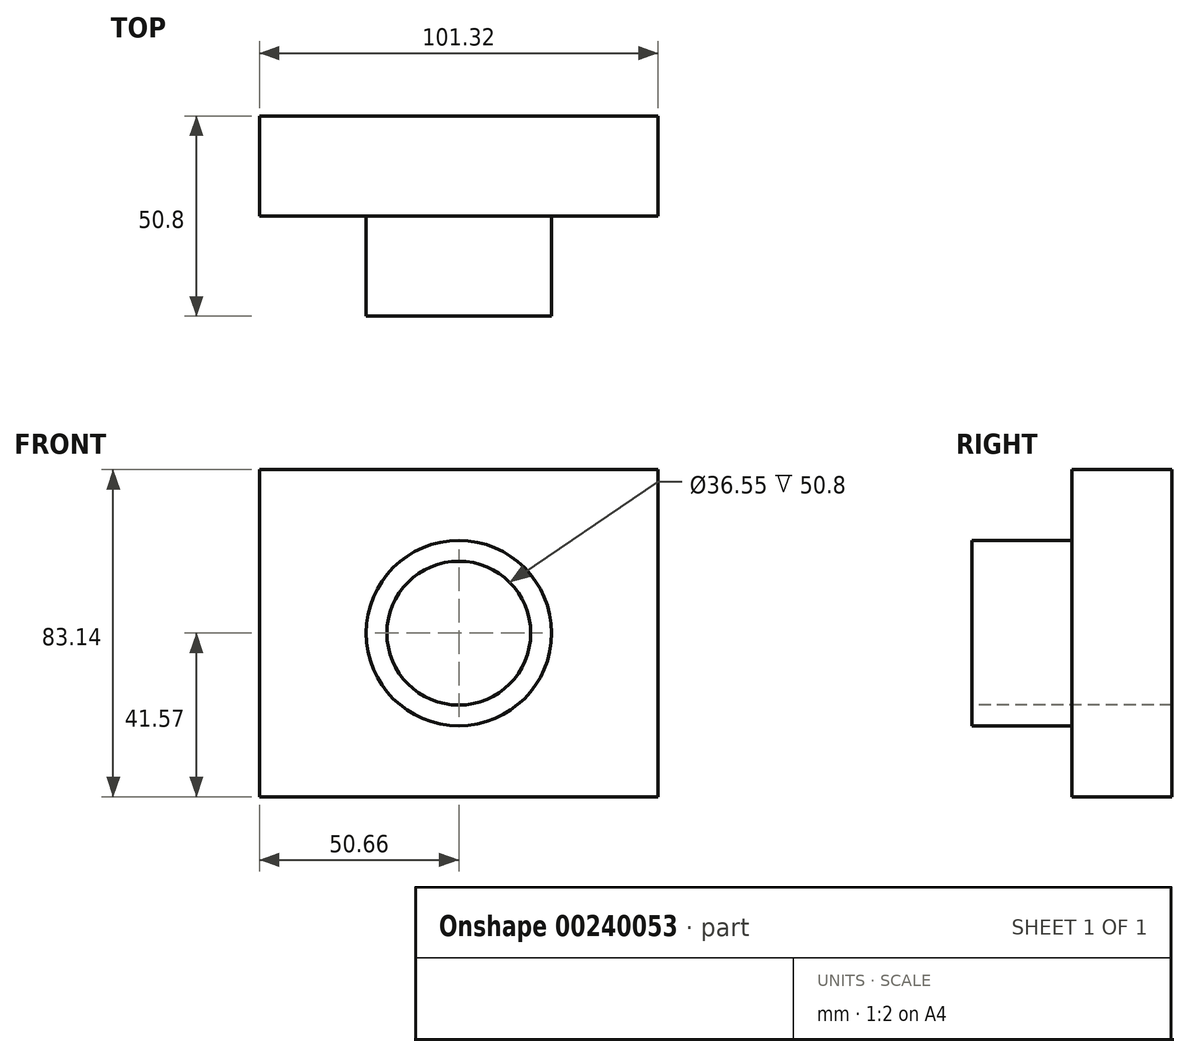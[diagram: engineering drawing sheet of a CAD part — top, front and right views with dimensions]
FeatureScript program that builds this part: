
annotation { "Feature Type Name" : "Feature", "Feature Type Description" : "" }
export const myFeature = defineFeature(function(context is Context, id is Id, definition is map)
    precondition{}
    {
        {
            var Q0;
            Q0=qCreatedBy(makeId("Front.planeOp"),FACE);
            var sketch = newSketch(context, id + "F0", { "sketchPlane" : qUnion([Q0])});
            skLineSegment(sketch, "E0.bottom", {"start": v(50.66, -41.57) * mm, "end": v(-50.66, -41.57) * mm});
            skLineSegment(sketch, "E0.top", {"start": v(50.66, 41.57) * mm, "end": v(-50.66, 41.57) * mm});
            skLineSegment(sketch, "E0.left", {"start": v(50.66, -41.57) * mm, "end": v(50.66, 41.57) * mm});
            skLineSegment(sketch, "E0.right", {"start": v(-50.66, -41.57) * mm, "end": v(-50.66, 41.57) * mm});
            skPoint(sketch, "E0.middle", {"position": v(0, 0) * mm});
            skSolve(sketch);
        }
        {
            var Q0;
            Q0=makeQuery(id+"F0.imprint","IMPRINT",FACE,{"disambiguationData":[TD([[makeQuery(id+"F0.imprint","IMPRINT",EDGE,{"derivedFrom":sQuery(id+"F0.wireOp",EDGE,"E0.bottom")}),-1.0]])]});
            extrude(context, id + "F1", {"entities" : qUnion([Q0]), "depth" : 25.4 * mm});
        }
        {
            var Q0;
            Q0=makeQuery(id+"F1.opExtrude","CAP_FACE",FACE,{"disambiguationData":[OSD([sQuery(id+"F0.wireOp",EDGE,"E0.bottom"),sQuery(id+"F0.wireOp",EDGE,"E0.top"),sQuery(id+"F0.wireOp",EDGE,"E0.left"),sQuery(id+"F0.wireOp",EDGE,"E0.right")])],"isStart":false});
            var sketch = newSketch(context, id + "F2", { "sketchPlane" : qUnion([Q0])});
            skCircle(sketch, "E1", {"center": v(0, 0) * mm, "radius": 18.27 * mm});
            skSolve(sketch);
        }
        {
            var Q0;
            Q0=makeQuery(id+"F2.imprint","IMPRINT",FACE,{"disambiguationData":[TD([[makeQuery(id+"F2.imprint","IMPRINT",EDGE,{"derivedFrom":sQuery(id+"F2.wireOp",EDGE,"E1")}),1.0]])]});
            extrude(context, id + "F3", {"entities" : qUnion([Q0]), "operationType" : NewBodyOperationType.REMOVE, "oppositeDirection" : true, "depth" : 25.4 * mm});
        }
        {
            var Q0;
            Q0=makeQuery(id+"F1.opExtrude","CAP_FACE",FACE,{"disambiguationData":[OSD([sQuery(id+"F0.wireOp",EDGE,"E0.bottom"),sQuery(id+"F0.wireOp",EDGE,"E0.top"),sQuery(id+"F0.wireOp",EDGE,"E0.left"),sQuery(id+"F0.wireOp",EDGE,"E0.right")])],"isStart":false});
            var sketch = newSketch(context, id + "F4", { "sketchPlane" : qUnion([Q0])});
            skCircle(sketch, "E2", {"center": v(0, 0) * mm, "radius": 18.24 * mm});
            skCircle(sketch, "E3", {"center": v(0, 0) * mm, "radius": 23.54 * mm});
            skSolve(sketch);
        }
        {
            var Q0;
            Q0=makeQuery(id+"F4.imprint","IMPRINT",FACE,{"disambiguationData":[TD([[makeQuery(id+"F4.imprint","IMPRINT",EDGE,{"derivedFrom":sQuery(id+"F4.wireOp",EDGE,"E3")}),1.0]])]});
            extrude(context, id + "F5", {"entities" : qUnion([Q0]), "operationType" : NewBodyOperationType.ADD, "depth" : 25.4 * mm});
        }
    });
